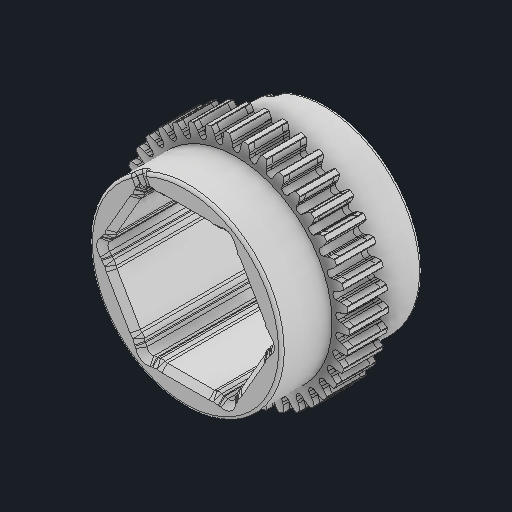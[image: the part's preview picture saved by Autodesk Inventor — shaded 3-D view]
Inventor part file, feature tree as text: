
AUTODESK INVENTOR PART (.ipt)
format: ipt  version: 2024 (Build 280153000, 153)  size: 2,020,352 bytes
history: native  units: in
note: dims shown in document units (in); Inventor stores cm internally (conversion verified against a paired STEP export)
features: fillet x1
ambient origin geometry x8: Origin, YZ Plane, XZ Plane, XY Plane, X Axis, Y Axis, Z Axis, Center Point
bodies: Solid1 (feature_tree)
feature tree (1):
  fillet  "Fillet5"  [1 undecoded]
note: 1 required parameter value undecoded (feature->parameter linkage not recoverable at this tier; creation-order binding heuristic only, values carry confidence <= 0.55)
